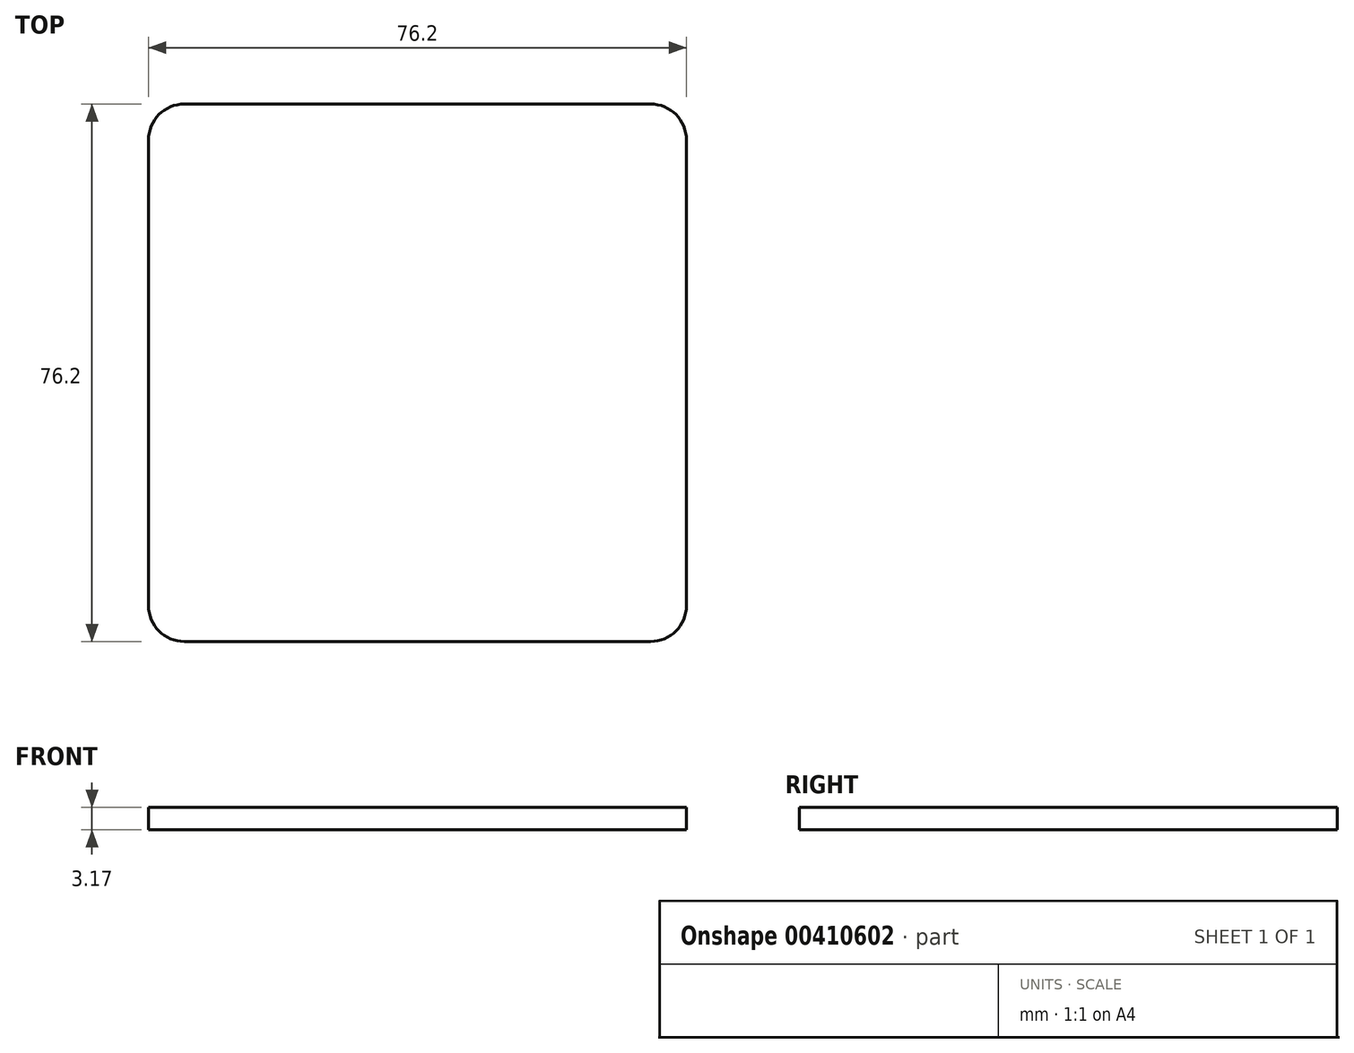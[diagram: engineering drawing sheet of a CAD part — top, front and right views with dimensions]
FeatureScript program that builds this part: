
annotation { "Feature Type Name" : "Feature", "Feature Type Description" : "" }
export const myFeature = defineFeature(function(context is Context, id is Id, definition is map)
    precondition{}
    {
        {
            var Q0;
            Q0=qCreatedBy(makeId("Top.planeOp"),FACE);
            var sketch = newSketch(context, id + "F0", { "sketchPlane" : qUnion([Q0])});
            skLineSegment(sketch, "E0.bottom", {"start": v(-38.1, -38.1) * mm, "end": v(38.1, -38.1) * mm});
            skLineSegment(sketch, "E0.top", {"start": v(-38.1, 38.1) * mm, "end": v(38.1, 38.1) * mm});
            skLineSegment(sketch, "E0.left", {"start": v(-38.1, -38.1) * mm, "end": v(-38.1, 38.1) * mm});
            skLineSegment(sketch, "E0.right", {"start": v(38.1, -38.1) * mm, "end": v(38.1, 38.1) * mm});
            skPoint(sketch, "E0.middle", {"position": v(0, 0) * mm});
            skSolve(sketch);
        }
        {
            var Q0;
            Q0=makeQuery(id+"F0.imprint","IMPRINT",FACE,{"disambiguationData":[TD([[makeQuery(id+"F0.imprint","IMPRINT",EDGE,{"derivedFrom":sQuery(id+"F0.wireOp",EDGE,"E0.bottom")}),1.0]])]});
            extrude(context, id + "F1", {"entities" : qUnion([Q0]), "depth" : 3.17 * mm});
        }
        {
            var Q0;
            Q0=makeQuery(id+"F1.opExtrude","SWEPT_EDGE",EDGE,{"disambiguationData":[OSD([sQuery(id+"F0.wireOp",EDGE,"E0.bottom"),sQuery(id+"F0.wireOp",EDGE,"E0.left")])]});
            var Q1;
            Q1=makeQuery(id+"F1.opExtrude","SWEPT_EDGE",EDGE,{"disambiguationData":[OSD([sQuery(id+"F0.wireOp",EDGE,"E0.bottom"),sQuery(id+"F0.wireOp",EDGE,"E0.right")])]});
            var Q2;
            Q2=makeQuery(id+"F1.opExtrude","SWEPT_EDGE",EDGE,{"disambiguationData":[OSD([sQuery(id+"F0.wireOp",EDGE,"E0.top"),sQuery(id+"F0.wireOp",EDGE,"E0.right")])]});
            var Q3;
            Q3=makeQuery(id+"F1.opExtrude","SWEPT_EDGE",EDGE,{"disambiguationData":[OSD([sQuery(id+"F0.wireOp",EDGE,"E0.top"),sQuery(id+"F0.wireOp",EDGE,"E0.left")])]});
            fillet(context, id + "F2", {"entities" : qUnion([Q0, Q1, Q2, Q3]), "radius" : 5.08 * mm, "tangentPropagation" : true, "allowEdgeOverflow" : false});
        }
    });
